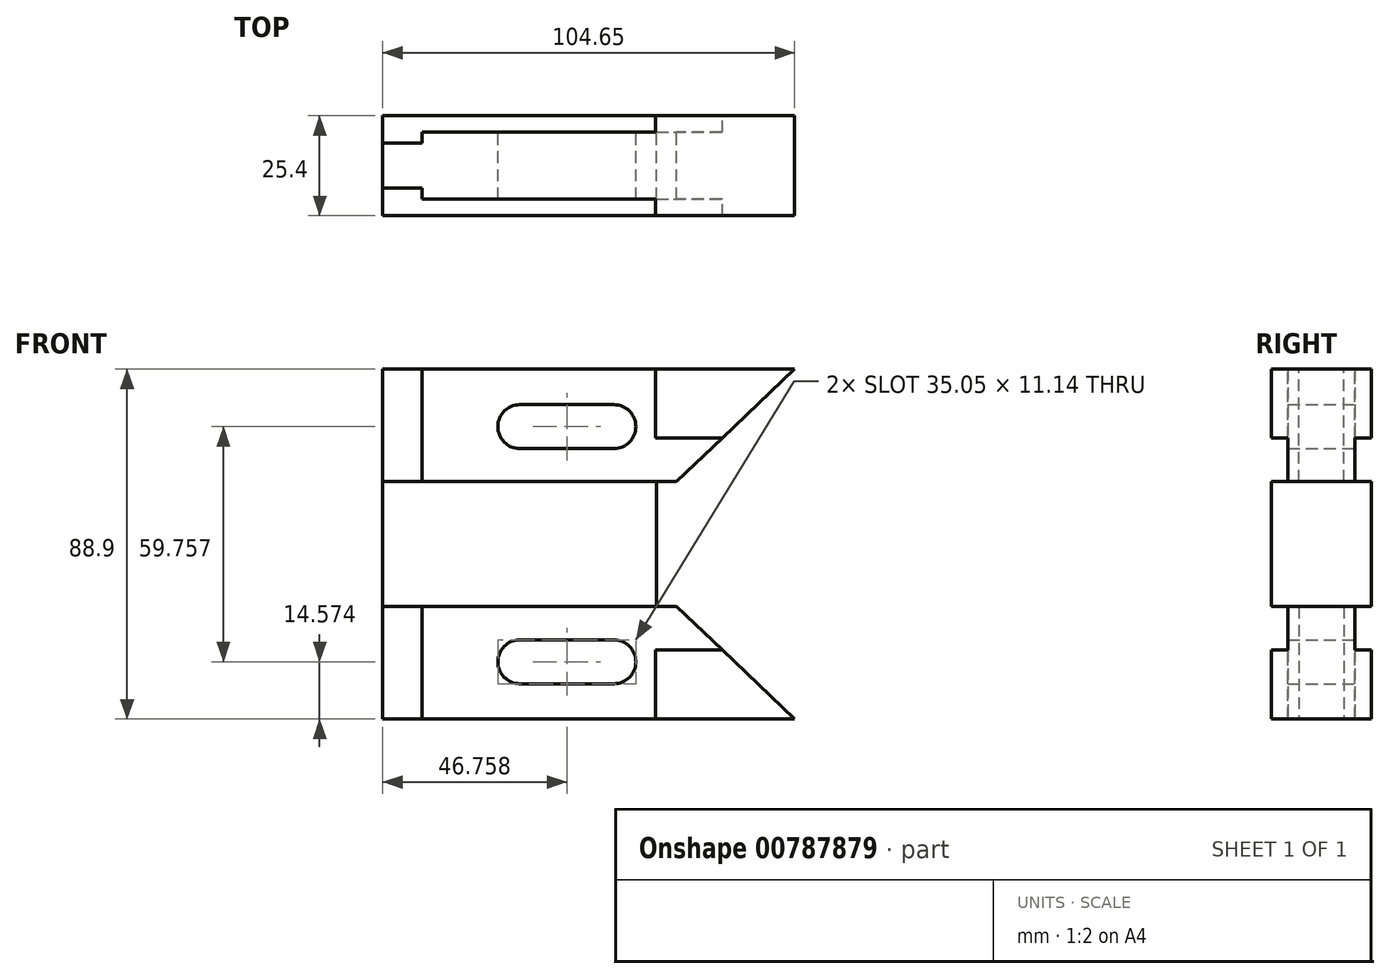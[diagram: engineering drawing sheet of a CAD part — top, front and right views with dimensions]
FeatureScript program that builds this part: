
annotation { "Feature Type Name" : "Feature", "Feature Type Description" : "" }
export const myFeature = defineFeature(function(context is Context, id is Id, definition is map)
    precondition{}
    {
        {
            var Q0;
            Q0=qCreatedBy(makeId("Front.planeOp"),FACE);
            var sketch = newSketch(context, id + "F0", { "sketchPlane" : qUnion([Q0])});
            skLineSegment(sketch, "E0.bottom", {"start": v(-34.8, 7.94) * mm, "end": v(34.8, 7.94) * mm});
            skLineSegment(sketch, "E0.top", {"start": v(-34.8, -7.94) * mm, "end": v(34.8, -7.94) * mm});
            skLineSegment(sketch, "E0.left", {"start": v(-34.8, 7.94) * mm, "end": v(-34.8, -7.94) * mm});
            skLineSegment(sketch, "E0.right", {"start": v(34.8, 7.94) * mm, "end": v(34.8, -7.94) * mm});
            skPoint(sketch, "E0.middle", {"position": v(0, 0) * mm});
            skLineSegment(sketch, "E1.bottom", {"start": v(-34.8, 7.94) * mm, "end": v(69.85, 7.94) * mm});
            skLineSegment(sketch, "E1.top", {"start": v(-34.8, 36.51) * mm, "end": v(69.85, 36.51) * mm});
            skLineSegment(sketch, "E1.left", {"start": v(-34.8, 7.94) * mm, "end": v(-34.8, 36.51) * mm});
            skLineSegment(sketch, "E1.right", {"start": v(69.85, 7.94) * mm, "end": v(69.85, 36.51) * mm});
            skLineSegment(sketch, "E2", {"start": v(69.85, 36.51) * mm, "end": v(39.88, 7.94) * mm});
            skLineSegment(sketch, "E3", {"start": v(-24.84, 36.51) * mm, "end": v(-24.84, 7.94) * mm});
            skLineSegment(sketch, "E4", {"start": v(-34.8, 22.23) * mm, "end": v(-10.16, 22.23) * mm});
            skCircle(sketch, "E5", {"center": v(0, 21.94) * mm, "radius": 5.57 * mm});
            skCircle(sketch, "E6", {"center": v(23.92, 21.94) * mm, "radius": 5.57 * mm});
            skLineSegment(sketch, "E7", {"start": v(0, 21.94) * mm, "end": v(23.92, 21.94) * mm});
            skLineSegment(sketch, "E8", {"start": v(0, 27.5) * mm, "end": v(23.92, 27.5) * mm});
            skLineSegment(sketch, "E9", {"start": v(0, 16.37) * mm, "end": v(23.92, 16.37) * mm});
            skLineSegment(sketch, "E10", {"start": v(34.45, 18.99) * mm, "end": v(51.47, 18.99) * mm});
            skLineSegment(sketch, "E11", {"start": v(34.45, 18.99) * mm, "end": v(34.45, 36.51) * mm});
            skSolve(sketch);
        }
        {
            var Q0;
            {var subQ4=sQuery(id+"F0.wireOp",EDGE,"E10");Q0=makeQuery(id+"F0.imprint","IMPRINT",FACE,{"disambiguationData":[TD([[makeQuery(id+"F0.imprint","IMPRINT",EDGE,{"derivedFrom":subQ4}),1.0]])]});}
            var Q1;
            Q1=makeQuery(id+"F0.imprint","IMPRINT",FACE,{"disambiguationData":[TD([[makeQuery(id+"F0.imprint","IMPRINT",EDGE,{"derivedFrom":sQuery(id+"F0.wireOp",EDGE,"E0.top")}),1.0]])]});
            extrude(context, id + "F1", {"entities" : qUnion([Q0, Q1]), "endBound" : BoundingType.SYMMETRIC, "depth" : 25.4 * mm, "offsetDistance" : 25.4 * mm});
        }
        {
            var Q0;
            {var subQ0=sQuery(id+"F0.wireOp",EDGE,"E8");Q0=makeQuery(id+"F0.imprint","IMPRINT",FACE,{"disambiguationData":[TD([[makeQuery(id+"F0.imprint","IMPRINT",EDGE,{"derivedFrom":subQ0}),1.0]])]});}
            extrude(context, id + "F2", {"entities" : qUnion([Q0]), "surfaceOperationType" : NewSurfaceOperationType.ADD, "endBound" : BoundingType.SYMMETRIC, "depth" : 17.02 * mm, "offsetDistance" : 25.4 * mm});
        }
        {
            var Q0;
            {var subQ0=sQuery(id+"F0.wireOp",EDGE,"E1.left");var subQ1=sQuery(id+"F0.wireOp",EDGE,"E1.top");var subQ2=makeQuery(id+"F0.imprint","INTERSECT",VERTEX,{"derivedFrom":[subQ1,subQ0]});Q0=makeQuery(id+"F0.imprint","IMPRINT",FACE,{"disambiguationData":[TD([[makeQuery(id+"F0.imprint","IMPRINT",EDGE,{"disambiguationData":[TD([[subQ2,-1.0]])],"derivedFrom":subQ1}),-1.0]])]});}
            var Q1;
            {var subQ1=sQuery(id+"F0.wireOp",EDGE,"E1.bottom");var subQ3=sQuery(id+"F0.wireOp",EDGE,"E3");var subQ4=makeQuery(id+"F0.imprint","INTERSECT",VERTEX,{"derivedFrom":[subQ1,subQ3]});Q1=makeQuery(id+"F0.imprint","IMPRINT",FACE,{"disambiguationData":[TD([[makeQuery(id+"F0.imprint","IMPRINT",EDGE,{"disambiguationData":[TD([[subQ4,1.0]])],"derivedFrom":subQ3}),-1.0]])]});}
            extrude(context, id + "F3", {"entities" : qUnion([Q0, Q1]), "endBound" : BoundingType.SYMMETRIC, "depth" : 11.43 * mm, "offsetDistance" : 25.4 * mm});
        }
        {
            var Q0;
            Q0=makeQuery(id+"F3.opExtrude","SWEPT_BODY",BODY,{"disambiguationData":[OSD([sQuery(id+"F0.wireOp",EDGE,"E1.bottom"),sQuery(id+"F0.wireOp",EDGE,"E1.top"),sQuery(id+"F0.wireOp",EDGE,"E1.left"),sQuery(id+"F0.wireOp",EDGE,"E3")])]});
            var Q1;
            Q1=makeQuery(id+"F2.opExtrude","SWEPT_BODY",BODY,{"disambiguationData":[OSD([sQuery(id+"F0.wireOp",EDGE,"E1.bottom"),sQuery(id+"F0.wireOp",EDGE,"E1.top"),sQuery(id+"F0.wireOp",EDGE,"E2"),sQuery(id+"F0.wireOp",EDGE,"E3"),sQuery(id+"F0.wireOp",EDGE,"E5"),sQuery(id+"F0.wireOp",EDGE,"E6"),sQuery(id+"F0.wireOp",EDGE,"E8"),sQuery(id+"F0.wireOp",EDGE,"E9"),sQuery(id+"F0.wireOp",EDGE,"E10"),sQuery(id+"F0.wireOp",EDGE,"E11")])]});
            var Q2;
            Q2=makeQuery(id+"F1.opExtrude","SWEPT_BODY",BODY,{"disambiguationData":[OSD([sQuery(id+"F0.wireOp",EDGE,"E1.top"),sQuery(id+"F0.wireOp",EDGE,"E2"),sQuery(id+"F0.wireOp",EDGE,"E10"),sQuery(id+"F0.wireOp",EDGE,"E11")])]});
            var Q3;
            Q3=makeQuery(id+"F1.opExtrude","SWEPT_BODY",BODY,{"disambiguationData":[OSD([sQuery(id+"F0.wireOp",EDGE,"E0.top"),sQuery(id+"F0.wireOp",EDGE,"E0.left"),sQuery(id+"F0.wireOp",EDGE,"E0.right"),sQuery(id+"F0.wireOp",EDGE,"E1.bottom")])]});
            var Q4;
            Q4=makeQuery(id+"F1.opExtrude","SWEPT_FACE",FACE,{"disambiguationData":[OSD([sQuery(id+"F0.wireOp",EDGE,"E0.top")])]});
            mirror(context, id + "F4", {"operationType" : NewBodyOperationType.ADD, "entities" : qUnion([Q0, Q1, Q2, Q3]), "mirrorPlane" : qUnion([Q4])});
        }
    });
